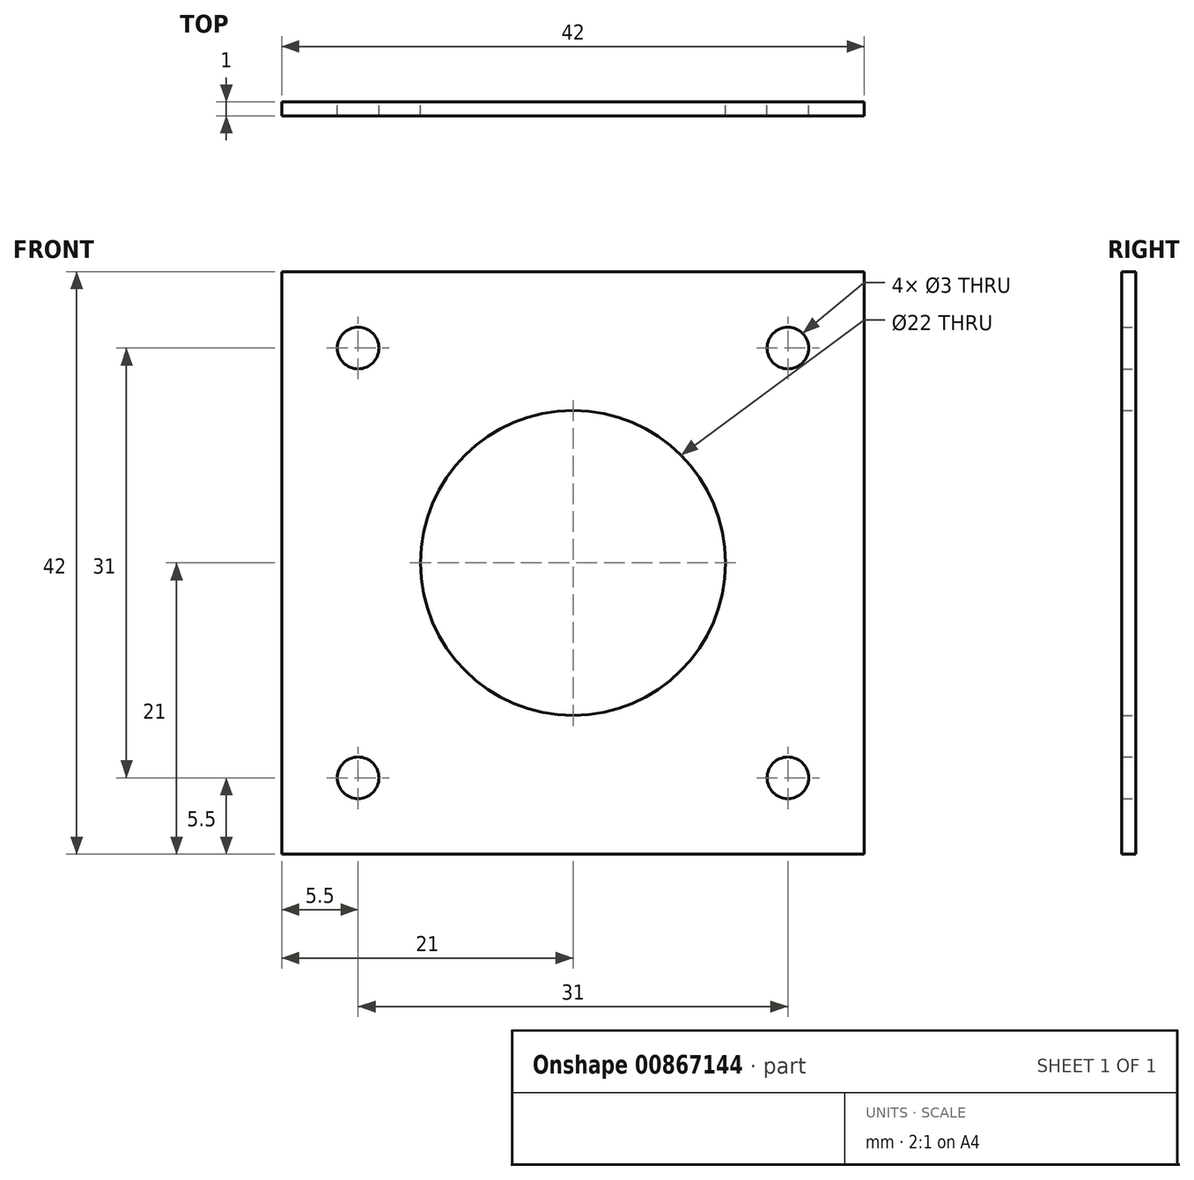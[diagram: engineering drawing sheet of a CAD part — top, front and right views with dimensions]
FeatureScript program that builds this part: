
annotation { "Feature Type Name" : "Feature", "Feature Type Description" : "" }
export const myFeature = defineFeature(function(context is Context, id is Id, definition is map)
    precondition{}
    {
        {
            var Q0;
            Q0=qCreatedBy(makeId("Front.planeOp"),FACE);
            var sketch = newSketch(context, id + "F0", { "sketchPlane" : qUnion([Q0])});
            skCircle(sketch, "E0", {"center": v(0, 0) * mm, "radius": 1.5 * mm});
            skCircle(sketch, "E1.0.1.0", {"center": v(0, 31) * mm, "radius": 1.5 * mm});
            skCircle(sketch, "E1.1.0.0", {"center": v(31, 0) * mm, "radius": 1.5 * mm});
            skCircle(sketch, "E1.1.1.0", {"center": v(31, 31) * mm, "radius": 1.5 * mm});
            skLineSegment(sketch, "E1.direction1", {"start": v(0, 0) * mm, "end": v(31, 0) * mm, "construction": true});
            skLineSegment(sketch, "E1.direction2", {"start": v(0, 0) * mm, "end": v(0, 31) * mm, "construction": true});
            skLineSegment(sketch, "E2", {"start": v(15.5, 0) * mm, "end": v(15.5, 31) * mm, "construction": true});
            skLineSegment(sketch, "E3.bottom", {"start": v(36.5, 36.5) * mm, "end": v(-5.5, 36.5) * mm});
            skLineSegment(sketch, "E3.top", {"start": v(36.5, -5.5) * mm, "end": v(-5.5, -5.5) * mm});
            skLineSegment(sketch, "E3.left", {"start": v(36.5, 36.5) * mm, "end": v(36.5, -5.5) * mm});
            skLineSegment(sketch, "E3.right", {"start": v(-5.5, 36.5) * mm, "end": v(-5.5, -5.5) * mm});
            skPoint(sketch, "E3.middle", {"position": v(15.5, 15.5) * mm});
            skCircle(sketch, "E4", {"center": v(15.5, 15.5) * mm, "radius": 11 * mm});
            skSolve(sketch);
        }
        {
            var Q0;
            Q0 = qSketchRegion(id + "F0", true);
            extrude(context, id + "F1", {"entities" : qUnion([Q0]), "depth" : 1 * mm, "offsetDistance" : 25 * mm});
        }
    });
